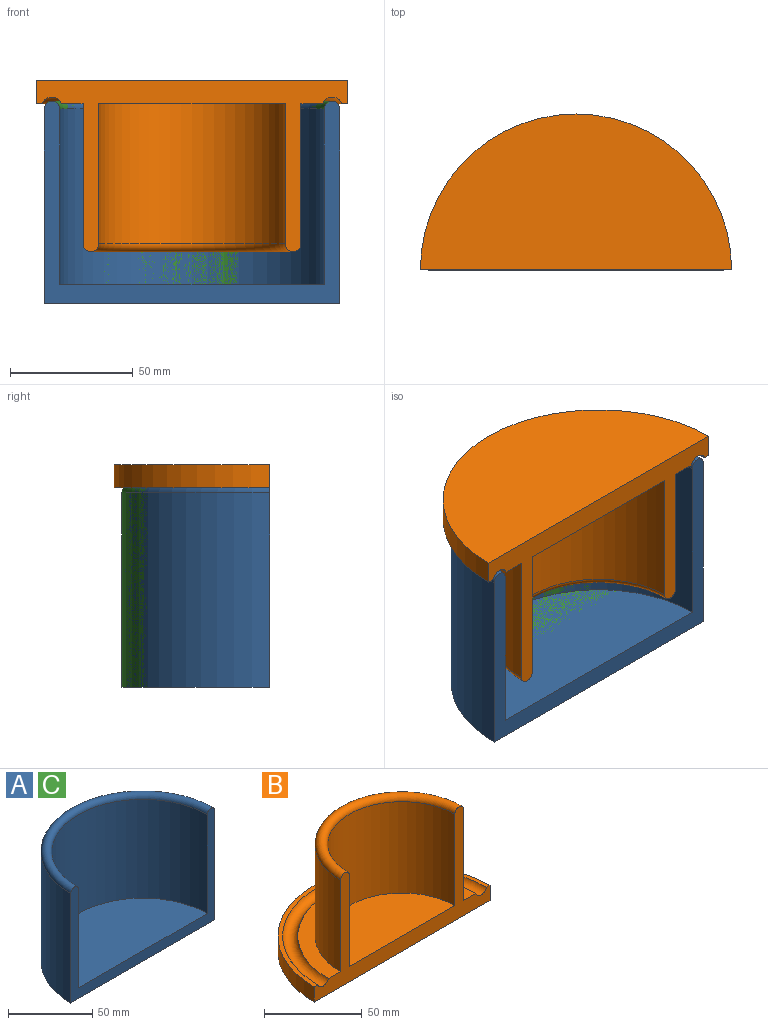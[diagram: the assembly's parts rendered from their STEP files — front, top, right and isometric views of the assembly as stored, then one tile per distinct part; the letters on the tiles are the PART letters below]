
ASSEMBLY  parts=3 mates=1
PART A: 6 faces, bbox 130.6x65.3x82.6 mm
  f0: plane 120.65x60.33mm, normal (0,0,-1), area 5716.3mm2, adj f1,f5
  f1: cylinder r=60.32mm len=120.65mm, axis (0,0,-1), area 15042.9mm2, adj f0,f2,f5
  f2: torus R=57.15mm, axis (0,0,-1), area 1790.9mm2, adj f1,f3,f5
  f3: cylinder r=53.98mm len=107.95mm, axis (0,0,-1), area 12146.9mm2, adj f2,f4,f5
  f4: plane 107.95x53.98mm, normal (0,0,1), area 4576.2mm2, adj f3,f5
  f5: plane 120.65x82.55mm, normal (0,-1,0), area 1875.3mm2, adj f0,f1,f2,f3,f4
PART B: 10 faces, bbox 132.5x66.3x69.9 mm
  f0: plane 127x63.5mm, normal (0,0,-1), area 6333.8mm2, adj f1,f9
  f1: cylinder r=63.5mm len=127mm, axis (0,0,-1), area 1900.2mm2, adj f0,f2,f9
  f2: plane 127x63.5mm, normal (0,0,1), area 486.9mm2, adj f1,f3,f9
  f3: torus R=57.15mm, axis (0,0,-1), area 1828.5mm2, adj f2,f4,f9
  f4: plane 106.58x53.29mm, normal (0,0,1), area 1357.1mm2, adj f3,f5,f9
  f5: cylinder r=44.45mm len=88.9mm, axis (0,0,-1), area 7980.6mm2, adj f4,f6,f9
  f6: torus R=41.27mm, axis (0,0,-1), area 1293.4mm2, adj f5,f7,f9
  f7: cylinder r=38.1mm len=76.2mm, axis (0,0,-1), area 6840.6mm2, adj f6,f8,f9
  f8: plane 76.2x38.1mm, normal (0,0,1), area 2280.2mm2, adj f7,f9
  f9: plane 127x69.85mm, normal (0,-1,0), area 1935.6mm2, adj f0,f1,f2,f3,f4,f5,f6,f7
PART C: same geometry as A
PLACE A at identity
PLACE B rot(axis=(0,1,0),180deg) t=(0,0,90.93)mm
PLACE C at identity
MATE fastened B.f1 <-> C.f1  axis (0,0,-1) through (0,0,81.4)mm
